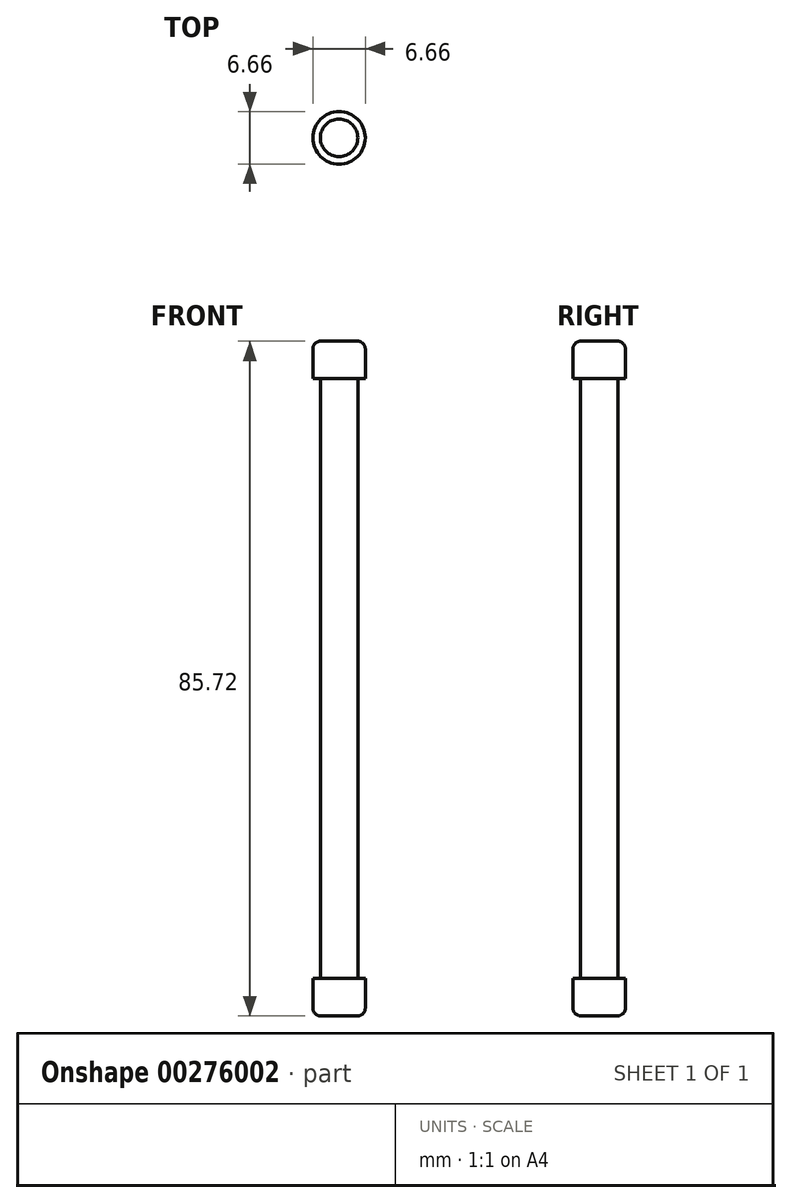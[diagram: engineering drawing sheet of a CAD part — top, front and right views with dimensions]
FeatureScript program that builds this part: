
annotation { "Feature Type Name" : "Feature", "Feature Type Description" : "" }
export const myFeature = defineFeature(function(context is Context, id is Id, definition is map)
    precondition{}
    {
        {
            var Q0;
            Q0=qCreatedBy(makeId("Top.planeOp"),FACE);
            var sketch = newSketch(context, id + "F0", { "sketchPlane" : qUnion([Q0])});
            skCircle(sketch, "E0", {"center": v(0, 0) * mm, "radius": 2.38 * mm});
            skCircle(sketch, "E1", {"center": v(0, 0) * mm, "radius": 3.33 * mm});
            skSolve(sketch);
        }
        {
            var Q0;
            Q0=qSketchRegion(id+"F0",true);
            extrude(context, id + "F1", {"entities" : qUnion([Q0]), "depth" : 4.76 * mm});
        }
        {
            var Q0;
            Q0=makeQuery(id+"F1.opExtrude","CAP_EDGE",EDGE,{"disambiguationData":[OSD([sQuery(id+"F0.wireOp",EDGE,"E1")])],"isStart":false});
            fillet(context, id + "F2", {"entities" : qUnion([Q0]), "radius" : 1.02 * mm, "tangentPropagation" : true, "allowEdgeOverflow" : false});
        }
        {
            var Q0;
            Q0=qCreatedBy(makeId("Top.planeOp"),FACE);
            var sketch = newSketch(context, id + "F3", { "sketchPlane" : qUnion([Q0])});
            skCircle(sketch, "E2", {"center": v(0, 0) * mm, "radius": 2.38 * mm});
            skSolve(sketch);
        }
        {
            var Q0;
            Q0 = qSketchRegion(id + "F3", true);
            extrude(context, id + "F4", {"entities" : qUnion([Q0]), "operationType" : NewBodyOperationType.ADD, "depth" : 4.76 * mm});
        }
        {
            var Q0;
            Q0 = qSketchRegion(id + "F3", true);
            extrude(context, id + "F5", {"entities" : qUnion([Q0]), "operationType" : NewBodyOperationType.ADD, "oppositeDirection" : true, "depth" : 80.96 * mm});
        }
        {
            var Q0;
            Q0=makeQuery(id+"F5.opExtrude","CAP_FACE",FACE,{"disambiguationData":[OSD([sQuery(id+"F3.wireOp",EDGE,"E2")])],"isStart":false});
            var sketch = newSketch(context, id + "F6", { "sketchPlane" : qUnion([Q0])});
            skCircle(sketch, "E3", {"center": v(0, 0) * mm, "radius": 3.33 * mm});
            skSolve(sketch);
        }
        {
            var Q0;
            Q0 = qSketchRegion(id + "F6", true);
            extrude(context, id + "F7", {"entities" : qUnion([Q0]), "operationType" : NewBodyOperationType.ADD, "oppositeDirection" : true, "depth" : 4.76 * mm});
        }
        {
            var Q0;
            Q0=makeQuery(id+"F7.boolean.opBoolean","MERGE",FACE,{"derivedFrom":[makeQuery(id+"F5.opExtrude","CAP_FACE",FACE,{"disambiguationData":[OSD([sQuery(id+"F3.wireOp",EDGE,"E2")])],"isStart":false}),makeQuery(id+"F7.opExtrude","CAP_FACE",FACE,{"disambiguationData":[OSD([sQuery(id+"F6.wireOp",EDGE,"E3")])],"isStart":true})]});
            fillet(context, id + "F8", {"entities" : qUnion([Q0]), "radius" : 1.02 * mm, "tangentPropagation" : true, "allowEdgeOverflow" : false});
        }
    });
